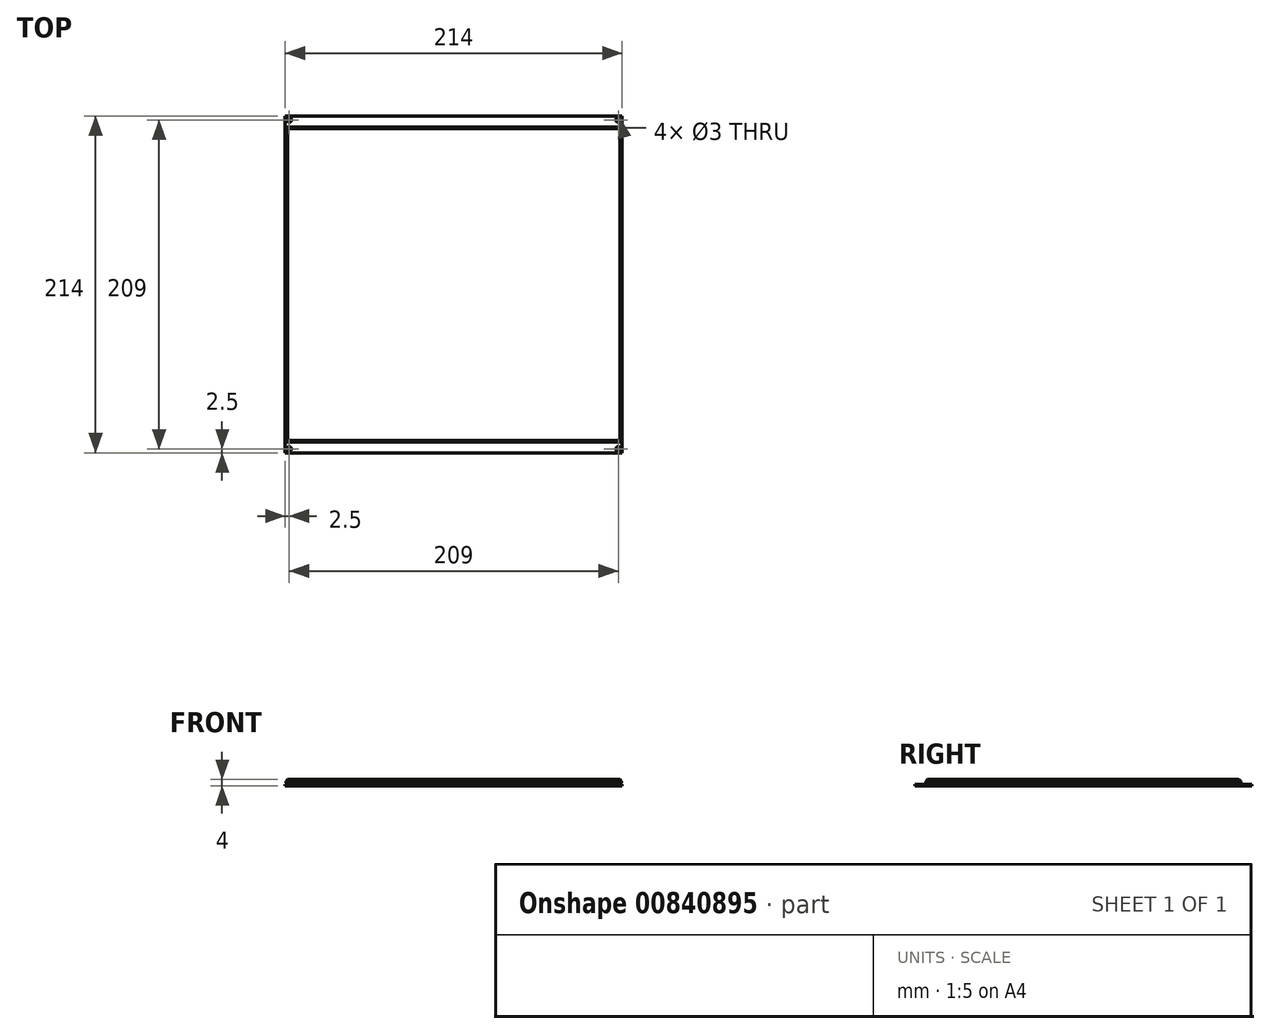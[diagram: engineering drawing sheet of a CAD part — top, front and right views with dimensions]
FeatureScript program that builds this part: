
annotation { "Feature Type Name" : "Feature", "Feature Type Description" : "" }
export const myFeature = defineFeature(function(context is Context, id is Id, definition is map)
    precondition{}
    {
        {
            var Q0;
            Q0=qCreatedBy(makeId("Top.planeOp"),FACE);
            var sketch = newSketch(context, id + "F0", { "sketchPlane" : qUnion([Q0])});
            skLineSegment(sketch, "E0.bottom", {"start": v(107, 107) * mm, "end": v(-107, 107) * mm});
            skLineSegment(sketch, "E0.top", {"start": v(107, -107) * mm, "end": v(-107, -107) * mm});
            skLineSegment(sketch, "E0.left", {"start": v(107, 107) * mm, "end": v(107, -107) * mm});
            skLineSegment(sketch, "E0.right", {"start": v(-107, 107) * mm, "end": v(-107, -107) * mm});
            skPoint(sketch, "E0.middle", {"position": v(0, 0) * mm});
            skCircle(sketch, "E1", {"center": v(-104.5, 104.5) * mm, "radius": 1.5 * mm});
            skLineSegment(sketch, "E2", {"start": v(0, -107) * mm, "end": v(0, 107) * mm, "construction": true});
            skLineSegment(sketch, "E3", {"start": v(-107, 0) * mm, "end": v(107, 0) * mm, "construction": true});
            skCircle(sketch, "E4.MirrorC", {"center": v(104.5, 104.5) * mm, "radius": 1.5 * mm});
            skCircle(sketch, "E5.MirrorC", {"center": v(-104.5, -104.5) * mm, "radius": 1.5 * mm});
            skCircle(sketch, "E6.MirrorC", {"center": v(104.5, -104.5) * mm, "radius": 1.5 * mm});
            skSolve(sketch);
        }
        {
            var Q0;
            Q0=qSketchRegion(id+"F0",true);
            extrude(context, id + "F1", {"entities" : qUnion([Q0]), "depth" : 1 * mm});
        }
        {
            var Q0;
            Q0=makeQuery(id+"F1.opExtrude","CAP_FACE",FACE,{"disambiguationData":[OSD([sQuery(id+"F0.wireOp",EDGE,"E0.bottom"),sQuery(id+"F0.wireOp",EDGE,"E0.top"),sQuery(id+"F0.wireOp",EDGE,"E0.left"),sQuery(id+"F0.wireOp",EDGE,"E0.right"),sQuery(id+"F0.wireOp",EDGE,"E1"),sQuery(id+"F0.wireOp",EDGE,"E4.MirrorC"),sQuery(id+"F0.wireOp",EDGE,"E5.MirrorC"),sQuery(id+"F0.wireOp",EDGE,"E6.MirrorC")])],"isStart":false});
            var sketch = newSketch(context, id + "F2", { "sketchPlane" : qUnion([Q0])});
            skLineSegment(sketch, "E7.bottom", {"start": v(-106.5, 100) * mm, "end": v(106.5, 100) * mm});
            skLineSegment(sketch, "E7.top", {"start": v(-106.5, -100) * mm, "end": v(106.5, -100) * mm});
            skLineSegment(sketch, "E7.left", {"start": v(-106.5, 100) * mm, "end": v(-106.5, -100) * mm});
            skLineSegment(sketch, "E7.right", {"start": v(106.5, 100) * mm, "end": v(106.5, -100) * mm});
            skSolve(sketch);
        }
        {
            var Q0;
            Q0 = qSketchRegion(id + "F2", true);
            extrude(context, id + "F3", {"entities" : qUnion([Q0]), "depth" : 3 * mm, "offsetDistance" : 25 * mm});
        }
        {
            var Q0;
            Q0=makeQuery(id+"F3.opExtrude","CAP_FACE",FACE,{"disambiguationData":[OSD([sQuery(id+"F2.wireOp",EDGE,"E7.bottom"),sQuery(id+"F2.wireOp",EDGE,"E7.top"),sQuery(id+"F2.wireOp",EDGE,"E7.left"),sQuery(id+"F2.wireOp",EDGE,"E7.right")])],"isStart":false});
            chamfer(context, id + "F4", {"entities" : qUnion([Q0]), "width" : 1 * mm, "tangentPropagation" : true});
        }
        {
            var Q0;
            Q0=makeQuery(id+"F3.opExtrude","CAP_FACE",FACE,{"disambiguationData":[OSD([sQuery(id+"F2.wireOp",EDGE,"E7.bottom"),sQuery(id+"F2.wireOp",EDGE,"E7.top"),sQuery(id+"F2.wireOp",EDGE,"E7.left"),sQuery(id+"F2.wireOp",EDGE,"E7.right")])],"isStart":true});
            chamfer(context, id + "F5", {"entities" : qUnion([Q0]), "width" : 1 * mm, "tangentPropagation" : true});
        }
    });
